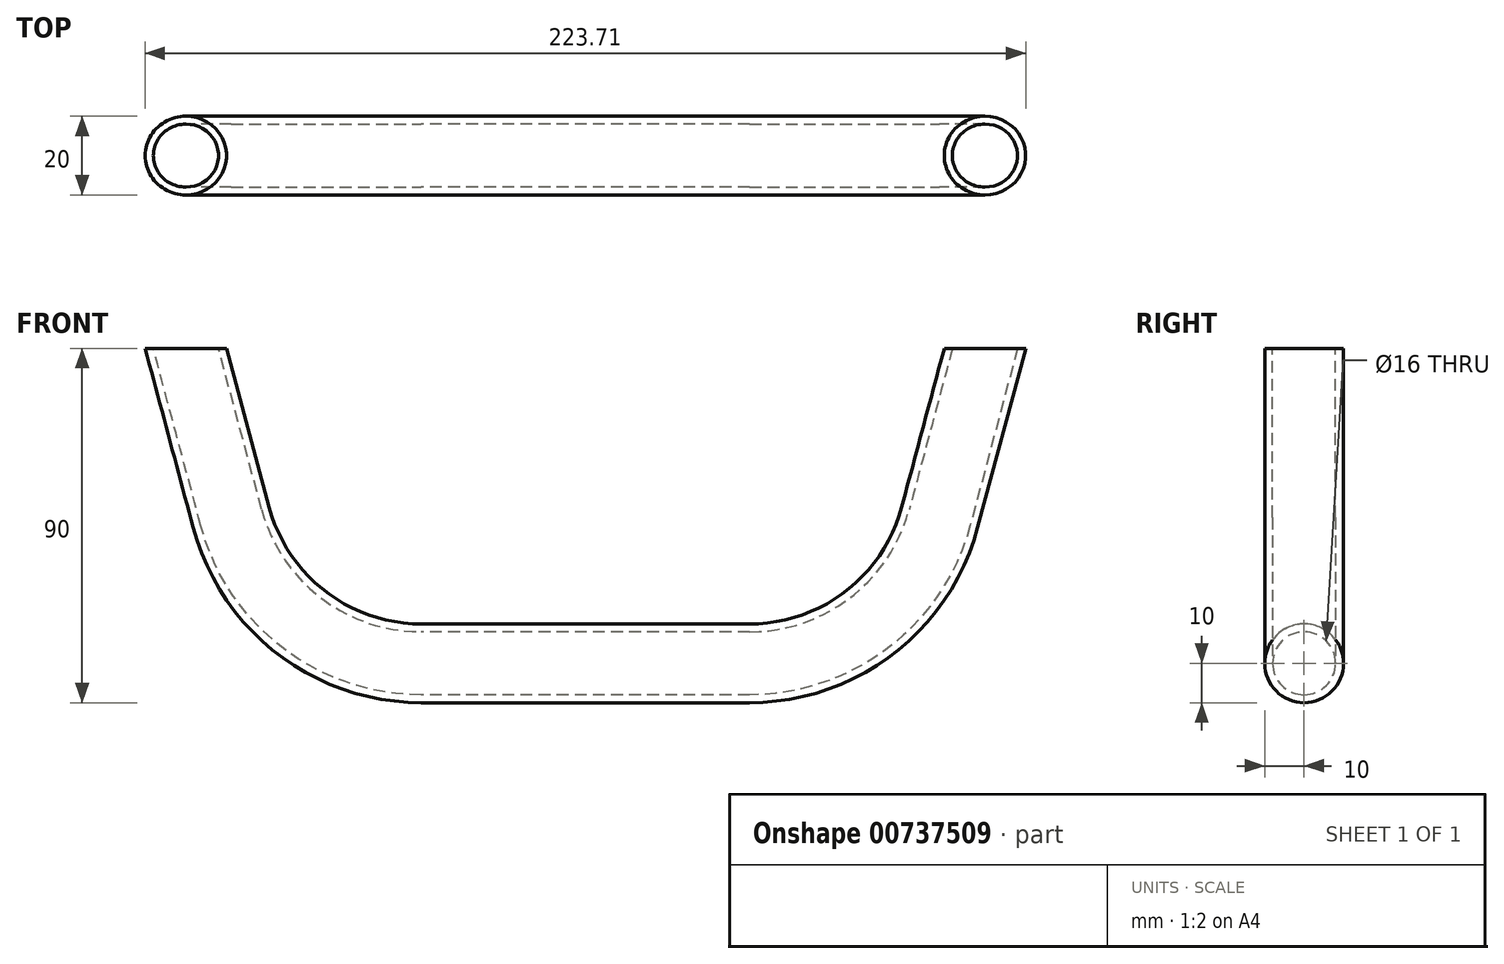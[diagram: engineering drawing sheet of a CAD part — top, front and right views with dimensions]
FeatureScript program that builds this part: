
annotation { "Feature Type Name" : "Feature", "Feature Type Description" : "" }
export const myFeature = defineFeature(function(context is Context, id is Id, definition is map)
    precondition{}
    {
        {
            var Q0;
            Q0=qCreatedBy(makeId("Front.planeOp"),FACE);
            var sketch = newSketch(context, id + "F0", { "sketchPlane" : qUnion([Q0])});
            skLineSegment(sketch, "E0", {"start": v(-38.37, 0) * mm, "end": v(-121.76, 0) * mm});
            skLineSegment(sketch, "E1", {"start": v(-170.06, 37.06) * mm, "end": v(-186.92, 100) * mm});
            skLineSegment(sketch, "E2", {"start": v(9.93, 37.06) * mm, "end": v(26.8, 100) * mm});
            skLineSegment(sketch, "E3", {"start": v(-181.56, 80) * mm, "end": v(21.44, 80) * mm, "construction": true});
            skPoint(sketch, "E4.visualSharp", {"position": v(0, 0) * mm});
            skArc(sketch, "E4.filletArc", {"start": v(-38.37, 0) * mm, "mid": v(-7.93, 10.33) * mm, "end": v(9.93, 37.06) * mm});
            skPoint(sketch, "E5.visualSharp", {"position": v(-160.13, 0) * mm});
            skArc(sketch, "E5.filletArc", {"start": v(-170.06, 37.06) * mm, "mid": v(-152.2, 10.33) * mm, "end": v(-121.76, 0) * mm});
            skSolve(sketch);
        }
        {
            var Q0;
            Q0=sQuery(id+"F0.wireOp",VERTEX,"E2.end");
            var Q1;
            Q1=sQuery(id+"F0.wireOp",EDGE,"E2");
            cPlane(context, id + "F1", {"entities" : qUnion([Q0, Q1]), "cplaneType" : CPlaneType.CURVE_POINT, "offset" : 25 * mm, "width" : 150 * mm, "height" : 150 * mm});
        }
        {
            var Q0;
            Q0=qCreatedBy(id+"F1.planeOp",FACE);
            var sketch = newSketch(context, id + "F2", { "sketchPlane" : qUnion([Q0])});
            skCircle(sketch, "E6", {"center": v(0, 0) * mm, "radius": 10 * mm});
            skCircle(sketch, "E7", {"center": v(0, 0) * mm, "radius": 8 * mm});
            skSolve(sketch);
        }
        {
            var Q0;
            Q0=makeQuery(id+"F2.imprint","IMPRINT",FACE,{"disambiguationData":[TD([[makeQuery(id+"F2.imprint","IMPRINT",EDGE,{"derivedFrom":sQuery(id+"F2.wireOp",EDGE,"E6")}),1.0]])]});
            var Q1;
            Q1=sQuery(id+"F0.wireOp",EDGE,"E2");
            var Q2;
            Q2=sQuery(id+"F0.wireOp",EDGE,"E4.filletArc");
            var Q3;
            Q3=sQuery(id+"F0.wireOp",EDGE,"E0");
            var Q4;
            Q4=sQuery(id+"F0.wireOp",EDGE,"E5.filletArc");
            var Q5;
            Q5=sQuery(id+"F0.wireOp",EDGE,"E1");
            sweep(context, id + "F3", {"profiles" : qUnion([Q0]), "path" : qUnion([Q1, Q2, Q3, Q4, Q5])});
        }
        {
            var Q0;
            Q0=qCreatedBy(makeId("Front.planeOp"),FACE);
            var sketch = newSketch(context, id + "F4", { "sketchPlane" : qUnion([Q0])});
            skLineSegment(sketch, "E8.bottom", {"start": v(-291.35, 164.62) * mm, "end": v(95.08, 164.62) * mm});
            skLineSegment(sketch, "E8.top", {"start": v(-291.35, 80) * mm, "end": v(95.08, 80) * mm});
            skLineSegment(sketch, "E8.left", {"start": v(-291.35, 164.62) * mm, "end": v(-291.35, 80) * mm});
            skLineSegment(sketch, "E8.right", {"start": v(95.08, 164.62) * mm, "end": v(95.08, 80) * mm});
            skSolve(sketch);
        }
        {
            var Q0;
            Q0=makeQuery(id+"F4.imprint","IMPRINT",FACE,{"disambiguationData":[TD([[makeQuery(id+"F4.imprint","IMPRINT",EDGE,{"derivedFrom":sQuery(id+"F4.wireOp",EDGE,"E8.bottom")}),-1.0]])]});
            extrude(context, id + "F5", {"entities" : qUnion([Q0]), "operationType" : NewBodyOperationType.REMOVE, "endBound" : BoundingType.THROUGH_ALL, "oppositeDirection" : true, "depth" : 25 * mm, "offsetDistance" : 25 * mm, "hasSecondDirection" : true, "secondDirectionBound" : SecondDirectionBoundingType.THROUGH_ALL, "secondDirectionOppositeDirection" : false, "secondDirectionDepth" : 25 * mm});
        }
    });
